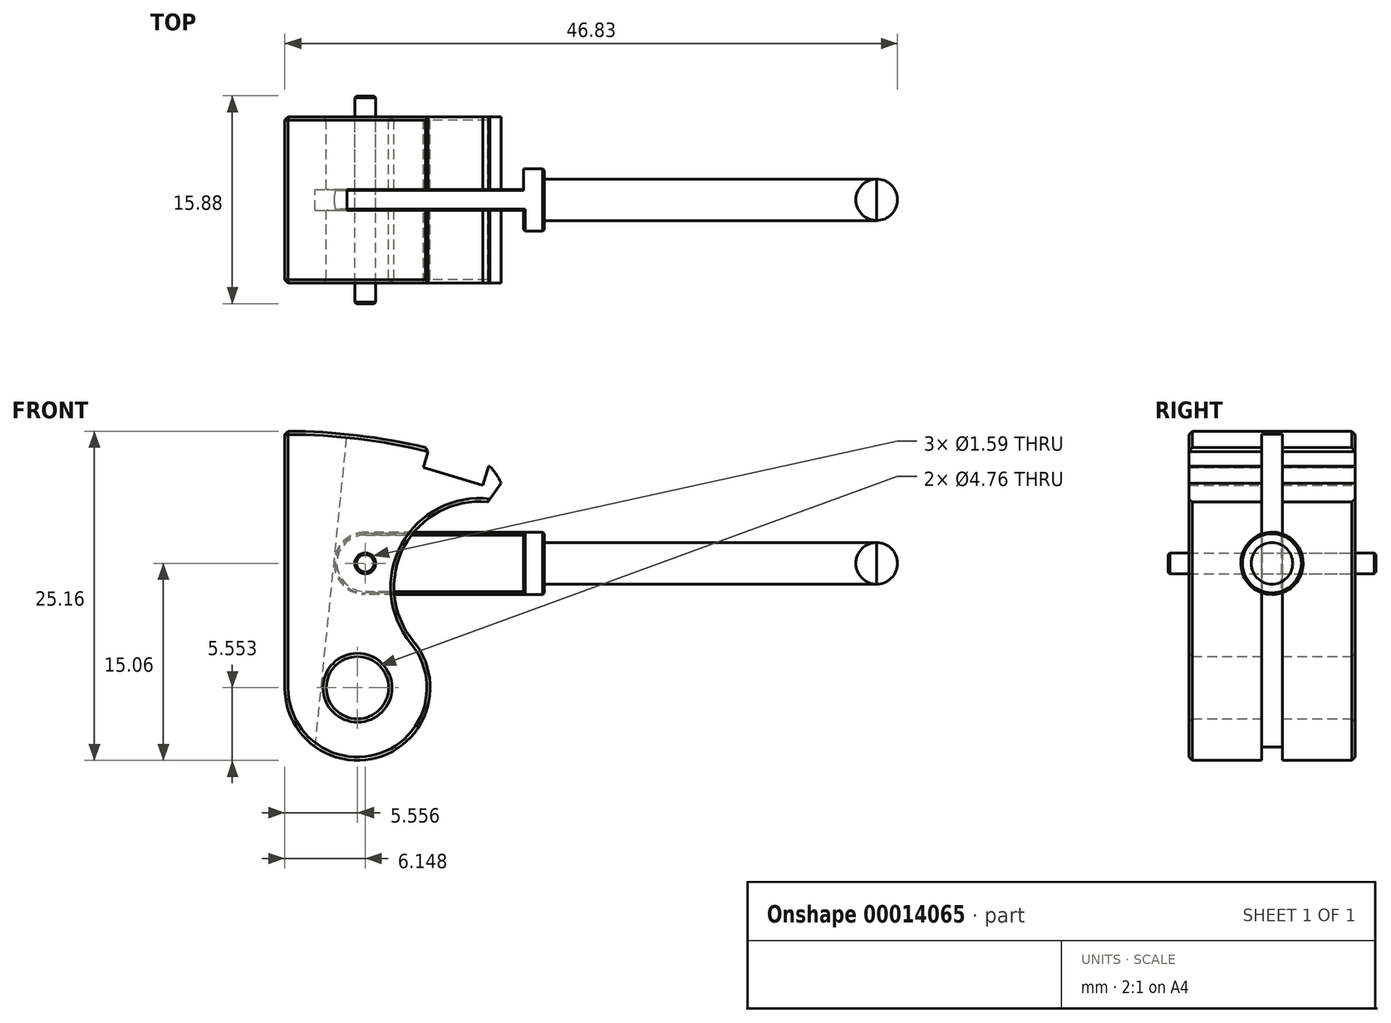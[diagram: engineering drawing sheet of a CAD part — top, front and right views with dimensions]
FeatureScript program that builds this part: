
annotation { "Feature Type Name" : "Feature", "Feature Type Description" : "" }
export const myFeature = defineFeature(function(context is Context, id is Id, definition is map)
    precondition{}
    {
        {
            var Q0;
            Q0=qCreatedBy(makeId("Front.planeOp"),FACE);
            var sketch = newSketch(context, id + "F0", { "sketchPlane" : qUnion([Q0])});
            skArc(sketch, "E0", {"start": v(18.35, 43.09) * mm, "mid": v(9.37, 45.89) * mm, "end": v(0, 46.83) * mm});
            skLineSegment(sketch, "E1", {"start": v(0, 46.83) * mm, "end": v(0, 0) * mm});
            skLineSegment(sketch, "E2", {"start": v(18.35, 43.09) * mm, "end": v(0, 0) * mm});
            skLineSegment(sketch, "E3", {"start": v(0, 0) * mm, "end": v(13.32, 44.9) * mm, "construction": true});
            skLineSegment(sketch, "E4.bottom", {"start": v(11.03, 45.58) * mm, "end": v(15.6, 44.22) * mm});
            skLineSegment(sketch, "E4.top", {"start": v(10.58, 44.06) * mm, "end": v(15.15, 42.7) * mm});
            skLineSegment(sketch, "E4.left", {"start": v(11.03, 45.58) * mm, "end": v(10.58, 44.06) * mm});
            skLineSegment(sketch, "E4.right", {"start": v(15.6, 44.22) * mm, "end": v(15.15, 42.7) * mm});
            skLineSegment(sketch, "E5", {"start": v(0, 0) * mm, "end": v(9.37, 45.89) * mm, "construction": true});
            skCircle(sketch, "E6", {"center": v(5.56, 27.22) * mm, "radius": 2.38 * mm});
            skCircle(sketch, "E7", {"center": v(12.11, 40.84) * mm, "radius": 4.86 * mm});
            skCircle(sketch, "E8", {"center": v(5.56, 27.22) * mm, "radius": 5.56 * mm});
            skCircle(sketch, "E9", {"center": v(14.87, 34.92) * mm, "radius": 6.53 * mm});
            skLineSegment(sketch, "E10", {"start": v(4.76, 46.6) * mm, "end": v(0, 0) * mm, "construction": true});
            skCircle(sketch, "E11", {"center": v(6.15, 36.73) * mm, "radius": 2.38 * mm, "construction": true});
            skCircle(sketch, "E12", {"center": v(6.15, 36.73) * mm, "radius": 0.8 * mm});
            skSolve(sketch);
        }
        {
            var Q0;
            {var subQ1=sQuery(id+"F0.wireOp",EDGE,"22ec3235-10a2-45b8-b53a-2e8e373b2cff.left");var subQ5=sQuery(id+"F0.wireOp",EDGE,"E6");var subQ7=makeQuery(id+"F0.imprint","INTERSECT",VERTEX,{"disambiguationData":[OD(0.0)],"derivedFrom":[subQ5,subQ1]});Q0=makeQuery(id+"F0.imprint","IMPRINT",FACE,{"disambiguationData":[TD([[makeQuery(id+"F0.imprint","IMPRINT",EDGE,{"disambiguationData":[TD([[subQ7,-1.0]])],"derivedFrom":subQ5}),-1.0]])]});}
            var Q1;
            {var subQ1=sQuery(id+"F0.wireOp",EDGE,"22ec3235-10a2-45b8-b53a-2e8e373b2cff.left");var subQ5=sQuery(id+"F0.wireOp",EDGE,"E6");var subQ7=makeQuery(id+"F0.imprint","INTERSECT",VERTEX,{"disambiguationData":[OD(0.0)],"derivedFrom":[subQ5,subQ1]});Q1=makeQuery(id+"F0.imprint","IMPRINT",FACE,{"disambiguationData":[TD([[makeQuery(id+"F0.imprint","IMPRINT",EDGE,{"disambiguationData":[TD([[subQ7,1.0]])],"derivedFrom":subQ5}),-1.0]])]});}
            var Q2;
            {var subQ7=sQuery(id+"F0.wireOp",EDGE,"E4.top");Q2=makeQuery(id+"F0.imprint","IMPRINT",FACE,{"disambiguationData":[TD([[makeQuery(id+"F0.imprint","IMPRINT",EDGE,{"derivedFrom":subQ7}),-1.0]])]});}
            var Q3;
            {var subQ3=sQuery(id+"F0.wireOp",EDGE,"E1");var subQ5=sQuery(id+"F0.wireOp",EDGE,"E0");var subQ7=makeQuery(id+"F0.imprint","INTERSECT",VERTEX,{"derivedFrom":[subQ5,subQ3]});Q3=makeQuery(id+"F0.imprint","IMPRINT",FACE,{"disambiguationData":[TD([[makeQuery(id+"F0.imprint","IMPRINT",EDGE,{"disambiguationData":[TD([[subQ7,-1.0]])],"derivedFrom":subQ3}),1.0]])]});}
            var Q4;
            Q4=makeQuery(id+"F0.imprint","IMPRINT",FACE,{"disambiguationData":[TD([[makeQuery(id+"F0.imprint","IMPRINT",EDGE,{"derivedFrom":sQuery(id+"F0.wireOp",EDGE,"E6")}),-1.0]])]});
            extrude(context, id + "F1", {"entities" : qUnion([Q0, Q1, Q2, Q3, Q4]), "endBound" : BoundingType.SYMMETRIC, "depth" : 12.7 * mm});
        }
        {
            var Q0;
            Q0=qCreatedBy(makeId("Front.planeOp"),FACE);
            var sketch = newSketch(context, id + "F14", { "sketchPlane" : qUnion([Q0])});
            skLineSegment(sketch, "E13.bottom", {"start": v(13.8, -1.41) * mm, "end": v(0, 0) * mm});
            skLineSegment(sketch, "E13.top", {"start": v(18.57, 45.18) * mm, "end": v(4.76, 46.6) * mm});
            skLineSegment(sketch, "E13.left", {"start": v(13.8, -1.41) * mm, "end": v(18.57, 45.18) * mm});
            skLineSegment(sketch, "E13.right", {"start": v(0, 0) * mm, "end": v(4.76, 46.6) * mm});
            skSolve(sketch);
        }
        {
            var Q0;
            Q0=qSketchRegion(id+"F14",true);
            extrude(context, id + "F2", {"entities" : qUnion([Q0]), "operationType" : NewBodyOperationType.REMOVE, "endBound" : BoundingType.SYMMETRIC, "oppositeDirection" : true, "depth" : 1.59 * mm});
        }
        {
            var Q0;
            Q0=qCreatedBy(makeId("Front.planeOp"),FACE);
            var sketch = newSketch(context, id + "F15", { "sketchPlane" : qUnion([Q0])});
            skLineSegment(sketch, "E14", {"start": v(3.77, 36.73) * mm, "end": v(6.15, 36.73) * mm, "construction": true});
            skArc(sketch, "E15", {"start": v(6.15, 39.11) * mm, "mid": v(4.46, 38.41) * mm, "end": v(3.77, 36.73) * mm});
            skLineSegment(sketch, "E16.bottom", {"start": v(19.84, 39.11) * mm, "end": v(19.84, 38.32) * mm});
            skLineSegment(sketch, "E16.left", {"start": v(19.84, 39.11) * mm, "end": v(6.15, 39.11) * mm});
            skLineSegment(sketch, "E17.rect.top", {"start": v(45.24, 38.32) * mm, "end": v(45.24, 36.73) * mm});
            skLineSegment(sketch, "E17.rect.left", {"start": v(19.84, 38.32) * mm, "end": v(45.24, 38.32) * mm});
            skLineSegment(sketch, "E18", {"start": v(3.77, 36.73) * mm, "end": v(45.24, 36.73) * mm});
            skArc(sketch, "E19", {"start": v(45.24, 38.32) * mm, "mid": v(46.36, 37.85) * mm, "end": v(46.83, 36.73) * mm});
            skLineSegment(sketch, "E20", {"start": v(46.83, 36.73) * mm, "end": v(45.24, 36.73) * mm});
            skCircle(sketch, "E21", {"center": v(6.15, 36.73) * mm, "radius": 12.1 * mm, "construction": true});
            skLineSegment(sketch, "E22.bottom", {"start": v(-5.95, 48.83) * mm, "end": v(18.25, 48.83) * mm, "construction": true});
            skLineSegment(sketch, "E22.top", {"start": v(-5.95, 24.63) * mm, "end": v(18.25, 24.63) * mm, "construction": true});
            skLineSegment(sketch, "E22.left", {"start": v(-5.95, 48.83) * mm, "end": v(-5.95, 24.63) * mm, "construction": true});
            skLineSegment(sketch, "E22.right", {"start": v(18.25, 48.83) * mm, "end": v(18.25, 24.63) * mm, "construction": true});
            skArc(sketch, "E23", {"start": v(45.24, 38.32) * mm, "mid": v(44.12, 37.85) * mm, "end": v(43.65, 36.73) * mm});
            skSolve(sketch);
        }
        {
            var Q0;
            {var subQ2=sQuery(id+"F15.wireOp",EDGE,"E15");Q0=makeQuery(id+"F15.imprint","IMPRINT",FACE,{"disambiguationData":[TD([[makeQuery(id+"F15.imprint","IMPRINT",EDGE,{"derivedFrom":subQ2}),1.0]])]});}
            var Q1;
            Q1=sQuery(id+"F15.wireOp",EDGE,"E18");
            revolve(context, id + "F16", {"entities" : qUnion([Q0]), "axis" : qUnion([Q1]), "revolveType" : RevolveType.FULL});
        }
        {
            var Q0;
            Q0=makeQuery(id+"F0.imprint","IMPRINT",FACE,{"disambiguationData":[TD([[makeQuery(id+"F0.imprint","IMPRINT",EDGE,{"derivedFrom":sQuery(id+"F0.wireOp",EDGE,"E12")}),1.0]])]});
            extrude(context, id + "F3", {"entities" : qUnion([Q0]), "endBound" : BoundingType.SYMMETRIC, "depth" : 15.88 * mm});
        }
        {
            var Q0;
            Q0=makeQuery(id+"F3.opExtrude","SWEPT_BODY",BODY,{"disambiguationData":[OSD([sQuery(id+"F0.wireOp",EDGE,"E12")])]});
            var Q1;
            Q1=makeQuery(id+"F16.opRevolve","SWEPT_BODY",BODY,{"disambiguationData":[OSD([sQuery(id+"F15.wireOp",EDGE,"E15"),sQuery(id+"F15.wireOp",EDGE,"E16.bottom"),sQuery(id+"F15.wireOp",EDGE,"E16.left"),sQuery(id+"F15.wireOp",EDGE,"E17.rect.left"),sQuery(id+"F15.wireOp",EDGE,"E18"),sQuery(id+"F15.wireOp",EDGE,"E19"),sQuery(id+"F15.wireOp",EDGE,"E20")])]});
            booleanBodies(context, id + "F4", {"operationType" : BooleanOperationType.SUBTRACTION, "tools" : qUnion([Q0]), "targets" : qUnion([Q1]), "keepTools" : true});
        }
        {
            var Q0;
            Q0=makeQuery(id+"F2.boolean.opBoolean","COPY",FACE,{"derivedFrom":makeQuery(id+"F2.opExtrude","CAP_FACE",FACE,{"disambiguationData":[OSD([sQuery(id+"F14.wireOp",EDGE,"E13.bottom"),sQuery(id+"F14.wireOp",EDGE,"E13.top"),sQuery(id+"F14.wireOp",EDGE,"E13.left"),sQuery(id+"F14.wireOp",EDGE,"E13.right")])],"isStart":false})});
            var sketch = newSketch(context, id + "F5", { "sketchPlane" : qUnion([Q0])});
            skLineSegment(sketch, "E24.bottom", {"start": v(18.25, 48.83) * mm, "end": v(0, 48.83) * mm});
            skLineSegment(sketch, "E24.top", {"start": v(18.25, 0) * mm, "end": v(0, 0) * mm});
            skLineSegment(sketch, "E24.left", {"start": v(18.25, 48.83) * mm, "end": v(18.25, 0) * mm});
            skLineSegment(sketch, "E24.right", {"start": v(0, 48.83) * mm, "end": v(0, 0) * mm});
            skLineSegment(sketch, "E25.left", {"start": v(18.25, 0) * mm, "end": v(18.25, 48.83) * mm});
            skLineSegment(sketch, "E25.right", {"start": v(0, 0) * mm, "end": v(0, 48.83) * mm});
            skSolve(sketch);
        }
        {
            var Q0;
            Q0=makeQuery(id+"F2.boolean.opBoolean","COPY",FACE,{"derivedFrom":makeQuery(id+"F2.opExtrude","CAP_FACE",FACE,{"disambiguationData":[OSD([sQuery(id+"F14.wireOp",EDGE,"E13.bottom"),sQuery(id+"F14.wireOp",EDGE,"E13.top"),sQuery(id+"F14.wireOp",EDGE,"E13.left"),sQuery(id+"F14.wireOp",EDGE,"E13.right")])],"isStart":true})});
            var sketch = newSketch(context, id + "F6", { "sketchPlane" : qUnion([Q0])});
            skLineSegment(sketch, "E26.bottom", {"start": v(0, 0) * mm, "end": v(-18.25, 0) * mm});
            skLineSegment(sketch, "E26.top", {"start": v(0, 48.83) * mm, "end": v(-18.25, 48.83) * mm});
            skLineSegment(sketch, "E26.left", {"start": v(0, 0) * mm, "end": v(0, 48.83) * mm});
            skLineSegment(sketch, "E26.right", {"start": v(-18.25, 0) * mm, "end": v(-18.25, 48.83) * mm});
            skSolve(sketch);
        }
        {
            var Q0;
            {var subQ10=sQuery(id+"F5.wireOp",EDGE,"E24.top");Q0=makeQuery(id+"F5.imprint","IMPRINT",FACE,{"disambiguationData":[TD([[makeQuery(id+"F5.imprint","IMPRINT",EDGE,{"derivedFrom":subQ10}),-1.0]])]});}
            var Q1;
            {var subQ0=makeQuery(id+"F2.opExtrude","CAP_FACE",FACE,{"disambiguationData":[OSD([sQuery(id+"F14.wireOp",EDGE,"E13.bottom"),sQuery(id+"F14.wireOp",EDGE,"E13.top"),sQuery(id+"F14.wireOp",EDGE,"E13.left"),sQuery(id+"F14.wireOp",EDGE,"E13.right")])],"isStart":false});Q1=makeQuery(id+"F5.imprint","IMPRINT",FACE,{"disambiguationData":[TD([[makeQuery(id+"F5.imprint","IMPRINT",EDGE,{"derivedFrom":makeQuery(id+"F2.boolean.opBoolean","INTERSECT",EDGE,{"derivedFrom":[makeQuery(id+"F1.opExtrude","SWEPT_FACE",FACE,{"disambiguationData":[OSD([sQuery(id+"F0.wireOp",EDGE,"E12")])]}),subQ0]})}),-1.0]])]});}
            var Q2;
            {var subQ0=makeQuery(id+"F2.boolean.opBoolean","INTERSECT",EDGE,{"derivedFrom":[makeQuery(id+"F1.opExtrude","SWEPT_FACE",FACE,{"disambiguationData":[OSD([sQuery(id+"F0.wireOp",EDGE,"E6")])]}),makeQuery(id+"F2.opExtrude","CAP_FACE",FACE,{"disambiguationData":[OSD([sQuery(id+"F14.wireOp",EDGE,"E13.bottom"),sQuery(id+"F14.wireOp",EDGE,"E13.top"),sQuery(id+"F14.wireOp",EDGE,"E13.left"),sQuery(id+"F14.wireOp",EDGE,"E13.right")])],"isStart":false})]});Q2=makeQuery(id+"F5.imprint","IMPRINT",FACE,{"disambiguationData":[TD([[makeQuery(id+"F5.imprint","IMPRINT",EDGE,{"derivedFrom":subQ0}),1.0]])]});}
            extrude(context, id + "F17", {"entities" : qUnion([Q0, Q1, Q2]), "oppositeDirection" : true, "depth" : 25.4 * mm});
        }
        {
            var Q0;
            {var subQ0=makeQuery(id+"F2.opExtrude","CAP_FACE",FACE,{"disambiguationData":[OSD([sQuery(id+"F14.wireOp",EDGE,"E13.bottom"),sQuery(id+"F14.wireOp",EDGE,"E13.top"),sQuery(id+"F14.wireOp",EDGE,"E13.left"),sQuery(id+"F14.wireOp",EDGE,"E13.right")])],"isStart":true});Q0=makeQuery(id+"F6.imprint","IMPRINT",FACE,{"disambiguationData":[TD([[makeQuery(id+"F6.imprint","IMPRINT",EDGE,{"derivedFrom":makeQuery(id+"F2.boolean.opBoolean","INTERSECT",EDGE,{"derivedFrom":[makeQuery(id+"F1.opExtrude","SWEPT_FACE",FACE,{"disambiguationData":[OSD([sQuery(id+"F0.wireOp",EDGE,"E12")])]}),subQ0]})}),1.0]])]});}
            var Q1;
            {var subQ10=sQuery(id+"F6.wireOp",EDGE,"E26.bottom");Q1=makeQuery(id+"F6.imprint","IMPRINT",FACE,{"disambiguationData":[TD([[makeQuery(id+"F6.imprint","IMPRINT",EDGE,{"derivedFrom":subQ10}),-1.0]])]});}
            var Q2;
            {var subQ0=makeQuery(id+"F2.boolean.opBoolean","INTERSECT",EDGE,{"derivedFrom":[makeQuery(id+"F1.opExtrude","SWEPT_FACE",FACE,{"disambiguationData":[OSD([sQuery(id+"F0.wireOp",EDGE,"E6")])]}),makeQuery(id+"F2.opExtrude","CAP_FACE",FACE,{"disambiguationData":[OSD([sQuery(id+"F14.wireOp",EDGE,"E13.bottom"),sQuery(id+"F14.wireOp",EDGE,"E13.top"),sQuery(id+"F14.wireOp",EDGE,"E13.left"),sQuery(id+"F14.wireOp",EDGE,"E13.right")])],"isStart":true})]});Q2=makeQuery(id+"F6.imprint","IMPRINT",FACE,{"disambiguationData":[TD([[makeQuery(id+"F6.imprint","IMPRINT",EDGE,{"derivedFrom":subQ0}),-1.0]])]});}
            extrude(context, id + "F7", {"entities" : qUnion([Q0, Q1, Q2]), "oppositeDirection" : true, "depth" : 25.4 * mm});
        }
        {
            var Q0;
            Q0=makeQuery(id+"F17.opExtrude","SWEPT_BODY",BODY,{"disambiguationData":[OSD([sQuery(id+"F0.wireOp",EDGE,"E12"),sQuery(id+"F14.wireOp",EDGE,"E13.bottom"),sQuery(id+"F14.wireOp",EDGE,"E13.top"),sQuery(id+"F14.wireOp",EDGE,"E13.left"),sQuery(id+"F14.wireOp",EDGE,"E13.right"),sQuery(id+"F5.wireOp",EDGE,"E24.top"),sQuery(id+"F5.wireOp",EDGE,"E24.bottom"),sQuery(id+"F5.wireOp",EDGE,"E25.left"),sQuery(id+"F5.wireOp",EDGE,"E25.right")])]});
            var Q1;
            Q1=makeQuery(id+"F7.opExtrude","SWEPT_BODY",BODY,{"disambiguationData":[OSD([sQuery(id+"F0.wireOp",EDGE,"E12"),sQuery(id+"F14.wireOp",EDGE,"E13.bottom"),sQuery(id+"F14.wireOp",EDGE,"E13.top"),sQuery(id+"F14.wireOp",EDGE,"E13.left"),sQuery(id+"F14.wireOp",EDGE,"E13.right"),sQuery(id+"F6.wireOp",EDGE,"E26.bottom"),sQuery(id+"F6.wireOp",EDGE,"E26.top"),sQuery(id+"F6.wireOp",EDGE,"E26.left"),sQuery(id+"F6.wireOp",EDGE,"E26.right")])]});
            var Q2;
            Q2=makeQuery(id+"F16.opRevolve","SWEPT_BODY",BODY,{"disambiguationData":[OSD([sQuery(id+"F15.wireOp",EDGE,"E15"),sQuery(id+"F15.wireOp",EDGE,"E16.bottom"),sQuery(id+"F15.wireOp",EDGE,"E16.left"),sQuery(id+"F15.wireOp",EDGE,"E17.rect.left"),sQuery(id+"F15.wireOp",EDGE,"E18"),sQuery(id+"F15.wireOp",EDGE,"E19"),sQuery(id+"F15.wireOp",EDGE,"E20")])]});
            booleanBodies(context, id + "F8", {"operationType" : BooleanOperationType.SUBTRACTION, "tools" : qUnion([Q0, Q1]), "targets" : qUnion([Q2])});
        }
        {
            var Q0;
            Q0=makeQuery(id+"F1.opExtrude","SWEPT_EDGE",EDGE,{"disambiguationData":[OSD([sQuery(id+"F0.wireOp",EDGE,"E0"),sQuery(id+"F0.wireOp",EDGE,"E1")])]});
            var Q1;
            {var subQ0=sQuery(id+"F0.wireOp",EDGE,"E0");var subQ1=makeQuery(id+"F0.imprint","INTERSECT",VERTEX,{"disambiguationData":[OD(1.0)],"derivedFrom":[subQ0,sQuery(id+"F0.wireOp",EDGE,"E7")]});Q1=makeQuery(id+"F1.opExtrude","CAP_EDGE",EDGE,{"disambiguationData":[OSD([subQ0]),TDD([makeQuery(id+"F0.imprint","IMPRINT",EDGE,{"disambiguationData":[TD([[subQ1,1.0]])],"derivedFrom":subQ0}),makeQuery(id+"F0.imprint","IMPRINT",EDGE,{"disambiguationData":[TD([[makeQuery(id+"F0.imprint","INTERSECT",VERTEX,{"derivedFrom":[subQ0,sQuery(id+"F0.wireOp",EDGE,"E1")]}),1.0]])],"derivedFrom":subQ0})])],"isStart":true});}
            var Q2;
            {var subQ0=sQuery(id+"F0.wireOp",EDGE,"E0");var subQ1=makeQuery(id+"F0.imprint","INTERSECT",VERTEX,{"disambiguationData":[OD(1.0)],"derivedFrom":[subQ0,sQuery(id+"F0.wireOp",EDGE,"E7")]});Q2=makeQuery(id+"F1.opExtrude","CAP_EDGE",EDGE,{"disambiguationData":[OSD([subQ0]),TDD([makeQuery(id+"F0.imprint","IMPRINT",EDGE,{"disambiguationData":[TD([[subQ1,1.0]])],"derivedFrom":subQ0}),makeQuery(id+"F0.imprint","IMPRINT",EDGE,{"disambiguationData":[TD([[makeQuery(id+"F0.imprint","INTERSECT",VERTEX,{"derivedFrom":[subQ0,sQuery(id+"F0.wireOp",EDGE,"E1")]}),1.0]])],"derivedFrom":subQ0})])],"isStart":false});}
            var Q3;
            {var subQ0=sQuery(id+"F0.wireOp",EDGE,"E0");var subQ1=sQuery(id+"F0.wireOp",EDGE,"E4.left");Q3=makeQuery(id+"F2.boolean.opBoolean","SPLIT",EDGE,{"disambiguationData":[TD([makeQuery(id+"F2.opExtrude","CAP_FACE",FACE,{"disambiguationData":[OSD([sQuery(id+"F14.wireOp",EDGE,"E13.bottom"),sQuery(id+"F14.wireOp",EDGE,"E13.top"),sQuery(id+"F14.wireOp",EDGE,"E13.left"),sQuery(id+"F14.wireOp",EDGE,"E13.right")])],"isStart":false})])],"derivedFrom":makeQuery(id+"F1.opExtrude","SWEPT_EDGE",EDGE,{"disambiguationData":[OSD([subQ0,subQ1])]})});}
            var Q4;
            {var subQ0=sQuery(id+"F0.wireOp",EDGE,"E0");var subQ1=sQuery(id+"F0.wireOp",EDGE,"E4.left");Q4=makeQuery(id+"F2.boolean.opBoolean","SPLIT",EDGE,{"disambiguationData":[TD([makeQuery(id+"F2.opExtrude","CAP_FACE",FACE,{"disambiguationData":[OSD([sQuery(id+"F14.wireOp",EDGE,"E13.bottom"),sQuery(id+"F14.wireOp",EDGE,"E13.top"),sQuery(id+"F14.wireOp",EDGE,"E13.left"),sQuery(id+"F14.wireOp",EDGE,"E13.right")])],"isStart":true})])],"derivedFrom":makeQuery(id+"F1.opExtrude","SWEPT_EDGE",EDGE,{"disambiguationData":[OSD([subQ0,subQ1])]})});}
            var Q5;
            Q5=makeQuery(id+"F1.opExtrude","CAP_EDGE",EDGE,{"disambiguationData":[OSD([sQuery(id+"F0.wireOp",EDGE,"E1")])],"isStart":false});
            var Q6;
            Q6=makeQuery(id+"F1.opExtrude","CAP_EDGE",EDGE,{"disambiguationData":[OSD([sQuery(id+"F0.wireOp",EDGE,"E1")])],"isStart":true});
            chamfer(context, id + "F9", {"entities" : qUnion([Q0, Q1, Q2, Q3, Q4, Q5, Q6]), "width" : 0.25 * mm, "tangentPropagation" : true});
        }
        {
            var Q0;
            Q0=makeQuery(id+"F16.opRevolve","SWEPT_EDGE",EDGE,{"disambiguationData":[OSD([sQuery(id+"F15.wireOp",EDGE,"E16.bottom"),sQuery(id+"F15.wireOp",EDGE,"E16.left")])]});
            var Q1;
            Q1=makeQuery(id+"F8.opBoolean","INTERSECT",EDGE,{"derivedFrom":[makeQuery(id+"F16.opRevolve","SWEPT_FACE",FACE,{"disambiguationData":[OSD([sQuery(id+"F15.wireOp",EDGE,"E16.left")])]}),makeQuery(id+"F17.opExtrude","SWEPT_FACE",FACE,{"disambiguationData":[OSD([sQuery(id+"F5.wireOp",EDGE,"E25.left")])]})]});
            var Q2;
            Q2=makeQuery(id+"F8.opBoolean","INTERSECT",EDGE,{"disambiguationData":[OD(0.0)],"derivedFrom":[makeQuery(id+"F16.opRevolve","SWEPT_FACE",FACE,{"disambiguationData":[OSD([sQuery(id+"F15.wireOp",EDGE,"E16.left")])]}),makeQuery(id+"F17.opExtrude","CAP_FACE",FACE,{"disambiguationData":[OSD([sQuery(id+"F0.wireOp",EDGE,"E12"),sQuery(id+"F14.wireOp",EDGE,"E13.bottom"),sQuery(id+"F14.wireOp",EDGE,"E13.top"),sQuery(id+"F14.wireOp",EDGE,"E13.left"),sQuery(id+"F14.wireOp",EDGE,"E13.right"),sQuery(id+"F5.wireOp",EDGE,"E24.top"),sQuery(id+"F5.wireOp",EDGE,"E24.bottom"),sQuery(id+"F5.wireOp",EDGE,"E25.left"),sQuery(id+"F5.wireOp",EDGE,"E25.right")])],"isStart":true})]});
            var Q3;
            Q3=makeQuery(id+"F8.opBoolean","INTERSECT",EDGE,{"disambiguationData":[OD(0.0)],"derivedFrom":[makeQuery(id+"F16.opRevolve","SWEPT_FACE",FACE,{"disambiguationData":[OSD([sQuery(id+"F15.wireOp",EDGE,"E16.left")])]}),makeQuery(id+"F7.opExtrude","CAP_FACE",FACE,{"disambiguationData":[OSD([sQuery(id+"F0.wireOp",EDGE,"E12"),sQuery(id+"F14.wireOp",EDGE,"E13.bottom"),sQuery(id+"F14.wireOp",EDGE,"E13.top"),sQuery(id+"F14.wireOp",EDGE,"E13.left"),sQuery(id+"F14.wireOp",EDGE,"E13.right"),sQuery(id+"F6.wireOp",EDGE,"E26.bottom"),sQuery(id+"F6.wireOp",EDGE,"E26.top"),sQuery(id+"F6.wireOp",EDGE,"E26.left"),sQuery(id+"F6.wireOp",EDGE,"E26.right")])],"isStart":true})]});
            var Q4;
            Q4=makeQuery(id+"F8.opBoolean","INTERSECT",EDGE,{"derivedFrom":[makeQuery(id+"F16.opRevolve","SWEPT_FACE",FACE,{"disambiguationData":[OSD([sQuery(id+"F15.wireOp",EDGE,"E16.left")])]}),makeQuery(id+"F7.opExtrude","SWEPT_FACE",FACE,{"disambiguationData":[OSD([sQuery(id+"F6.wireOp",EDGE,"E26.right")])]})]});
            chamfer(context, id + "F10", {"entities" : qUnion([Q0, Q1, Q2, Q3, Q4]), "width" : 0.13 * mm, "tangentPropagation" : true});
        }
        {
            var Q0;
            Q0=makeQuery(id+"F3.opExtrude","CAP_EDGE",EDGE,{"disambiguationData":[OSD([sQuery(id+"F0.wireOp",EDGE,"E12")])],"isStart":true});
            var Q1;
            Q1=makeQuery(id+"F3.opExtrude","CAP_EDGE",EDGE,{"disambiguationData":[OSD([sQuery(id+"F0.wireOp",EDGE,"E12")])],"isStart":false});
            chamfer(context, id + "F11", {"entities" : qUnion([Q0, Q1]), "width" : 0.13 * mm, "tangentPropagation" : true});
        }
        {
            var Q0;
            Q0=makeQuery(id+"F1.opExtrude","CAP_EDGE",EDGE,{"disambiguationData":[OSD([sQuery(id+"F0.wireOp",EDGE,"E6")])],"isStart":false});
            var Q1;
            Q1=makeQuery(id+"F1.opExtrude","CAP_EDGE",EDGE,{"disambiguationData":[OSD([sQuery(id+"F0.wireOp",EDGE,"E6")])],"isStart":true});
            chamfer(context, id + "F12", {"entities" : qUnion([Q0, Q1]), "width" : 0.25 * mm, "tangentPropagation" : true});
        }
        {
            var Q0;
            Q0=makeQuery(id+"F15.imprint","IMPRINT",FACE,{"disambiguationData":[TD([[makeQuery(id+"F15.imprint","IMPRINT",EDGE,{"derivedFrom":sQuery(id+"F15.wireOp",EDGE,"E17.rect.top")}),1.0]])]});
            var Q1;
            {var subQ2=sQuery(id+"F15.wireOp",EDGE,"E17.rect.top");Q1=makeQuery(id+"F15.imprint","IMPRINT",FACE,{"disambiguationData":[TD([[makeQuery(id+"F15.imprint","IMPRINT",EDGE,{"derivedFrom":subQ2}),-1.0]])]});}
            var Q2;
            Q2=sQuery(id+"F15.wireOp",EDGE,"E20");
            revolve(context, id + "F18", {"entities" : qUnion([Q0, Q1]), "axis" : qUnion([Q2]), "revolveType" : RevolveType.FULL});
        }
        {
            var Q0;
            {var subQ0=sQuery(id+"F0.wireOp",EDGE,"E7");var subQ1=sQuery(id+"F0.wireOp",EDGE,"E9");Q0=makeQuery(id+"F2.boolean.opBoolean","SPLIT",EDGE,{"disambiguationData":[TD([makeQuery(id+"F2.opExtrude","CAP_FACE",FACE,{"disambiguationData":[OSD([sQuery(id+"F14.wireOp",EDGE,"E13.bottom"),sQuery(id+"F14.wireOp",EDGE,"E13.top"),sQuery(id+"F14.wireOp",EDGE,"E13.left"),sQuery(id+"F14.wireOp",EDGE,"E13.right")])],"isStart":true})])],"derivedFrom":makeQuery(id+"F1.opExtrude","SWEPT_EDGE",EDGE,{"disambiguationData":[OSD([subQ0,subQ1])]})});}
            var Q1;
            {var subQ0=sQuery(id+"F0.wireOp",EDGE,"E7");var subQ1=sQuery(id+"F0.wireOp",EDGE,"E9");Q1=makeQuery(id+"F2.boolean.opBoolean","SPLIT",EDGE,{"disambiguationData":[TD([makeQuery(id+"F2.opExtrude","CAP_FACE",FACE,{"disambiguationData":[OSD([sQuery(id+"F14.wireOp",EDGE,"E13.bottom"),sQuery(id+"F14.wireOp",EDGE,"E13.top"),sQuery(id+"F14.wireOp",EDGE,"E13.left"),sQuery(id+"F14.wireOp",EDGE,"E13.right")])],"isStart":false})])],"derivedFrom":makeQuery(id+"F1.opExtrude","SWEPT_EDGE",EDGE,{"disambiguationData":[OSD([subQ0,subQ1])]})});}
            chamfer(context, id + "F13", {"entities" : qUnion([Q0, Q1]), "width" : 1.02 * mm, "tangentPropagation" : true});
        }
    });
